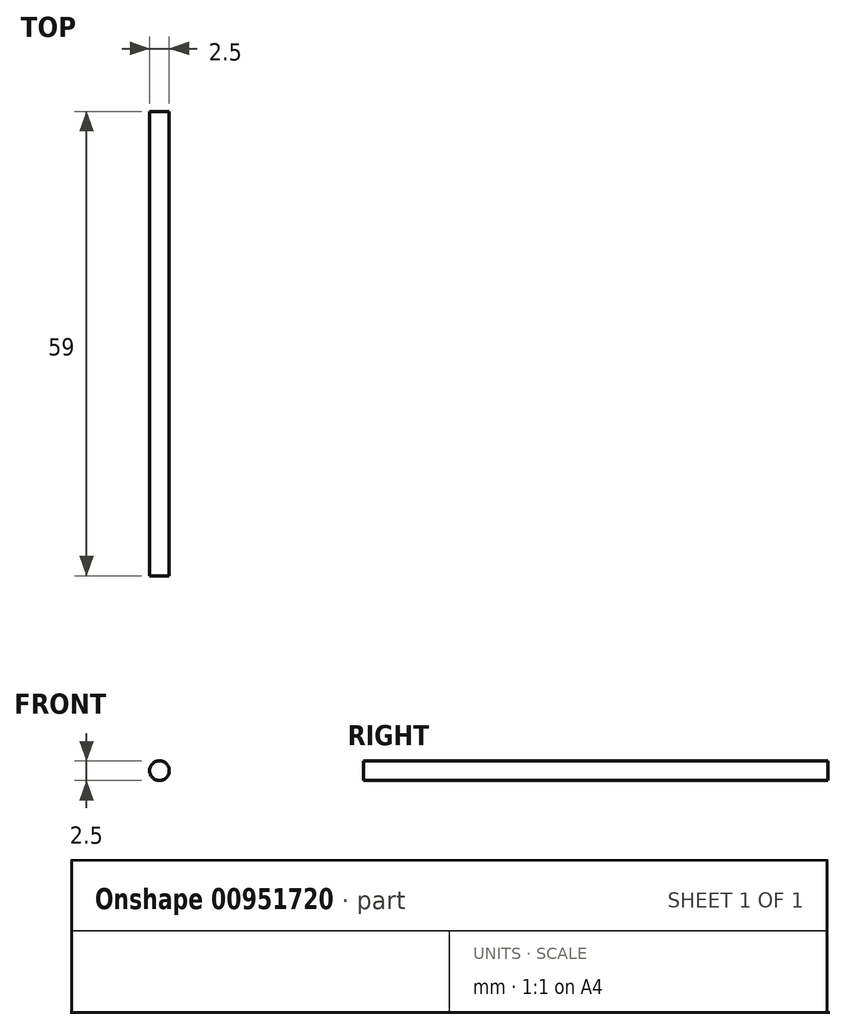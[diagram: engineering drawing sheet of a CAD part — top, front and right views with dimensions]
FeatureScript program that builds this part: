
annotation { "Feature Type Name" : "Feature", "Feature Type Description" : "" }
export const myFeature = defineFeature(function(context is Context, id is Id, definition is map)
    precondition{}
    {
        {
            var Q0;
            Q0=qCreatedBy(makeId("Front.planeOp"),FACE);
            var sketch = newSketch(context, id + "F0", { "sketchPlane" : qUnion([Q0])});
            skCircle(sketch, "E0", {"center": v(0, 0) * mm, "radius": 1.25 * mm});
            skSolve(sketch);
        }
        {
            var Q0;
            Q0=makeQuery(id+"F0.imprint","IMPRINT",FACE,{"disambiguationData":[TD([[makeQuery(id+"F0.imprint","IMPRINT",EDGE,{"derivedFrom":sQuery(id+"F0.wireOp",EDGE,"E0")}),1.0]])]});
            extrude(context, id + "F1", {"entities" : qUnion([Q0]), "depth" : 59 * mm, "offsetDistance" : 25 * mm});
        }
    });
